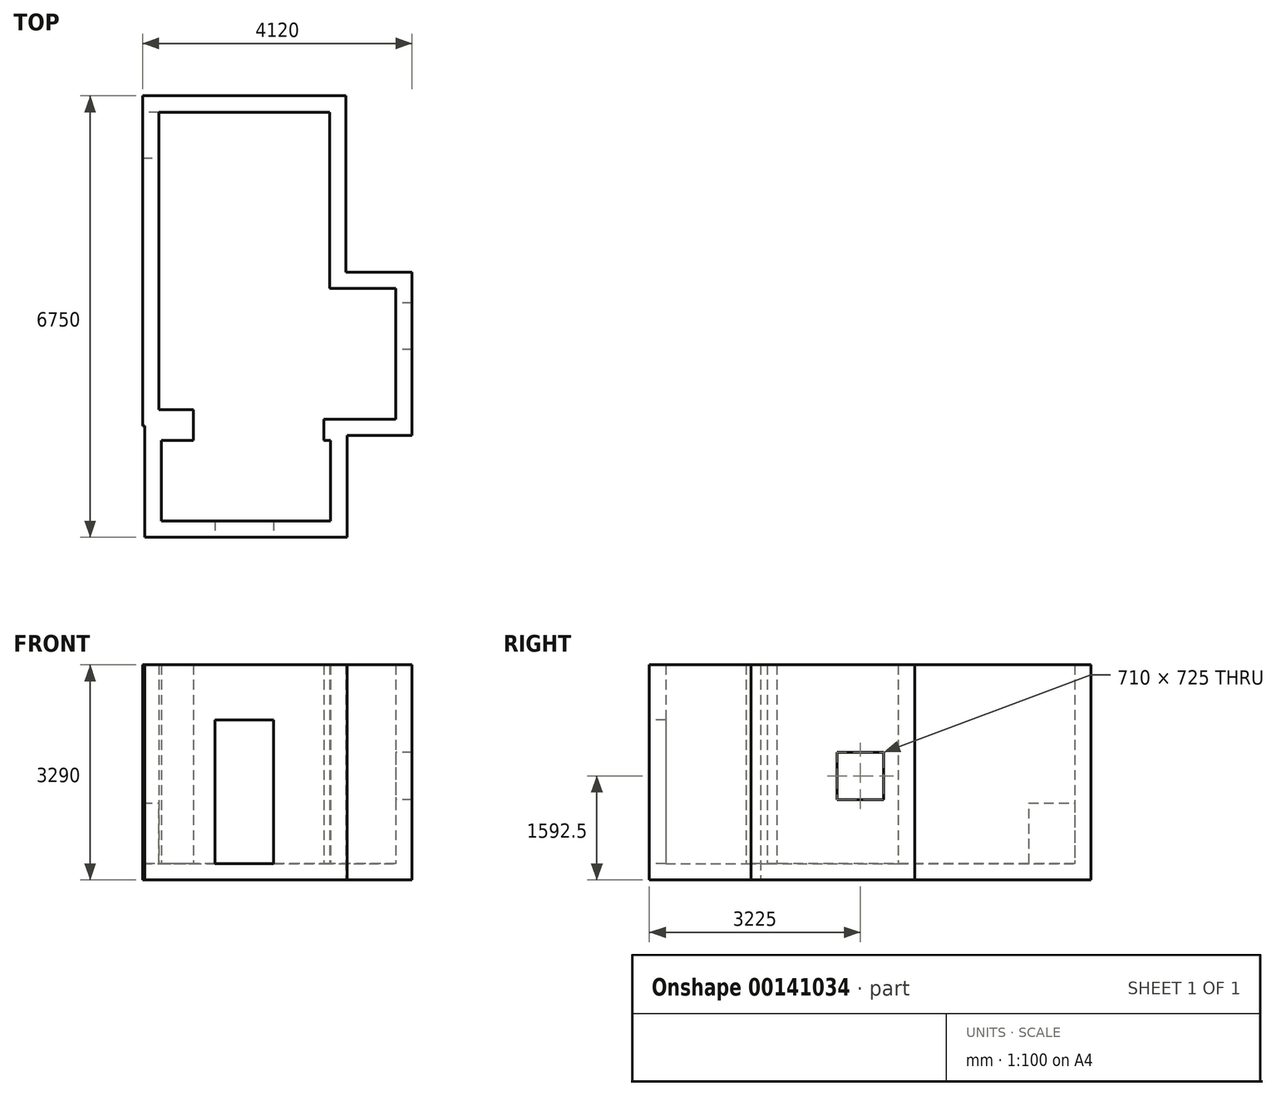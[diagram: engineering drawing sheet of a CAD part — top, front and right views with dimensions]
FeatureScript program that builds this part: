
annotation { "Feature Type Name" : "Feature", "Feature Type Description" : "" }
export const myFeature = defineFeature(function(context is Context, id is Id, definition is map)
    precondition{}
    {
        {
            var Q0;
            Q0=qCreatedBy(makeId("Top.planeOp"),FACE);
            var sketch = newSketch(context, id + "F0", { "sketchPlane" : qUnion([Q0])});
            skLineSegment(sketch, "E0", {"start": v(0, 0) * mm, "end": v(1649.99, 0) * mm});
            skLineSegment(sketch, "E1", {"start": v(1649.99, 0) * mm, "end": v(1649.99, 1230) * mm});
            skLineSegment(sketch, "E2", {"start": v(1649.99, 1230) * mm, "end": v(1544.99, 1230) * mm});
            skLineSegment(sketch, "E3", {"start": v(1544.99, 1230) * mm, "end": v(1544.99, 1555) * mm});
            skLineSegment(sketch, "E4", {"start": v(1544.99, 1555) * mm, "end": v(2644.99, 1555) * mm});
            skLineSegment(sketch, "E5", {"start": v(2644.99, 1555) * mm, "end": v(2644.99, 3555) * mm});
            skLineSegment(sketch, "E6", {"start": v(2644.99, 3555) * mm, "end": v(1634.99, 3555) * mm});
            skLineSegment(sketch, "E7", {"start": v(1634.99, 3555) * mm, "end": v(1634.99, 6250) * mm});
            skLineSegment(sketch, "E8", {"start": v(1634.99, 6250) * mm, "end": v(-975.01, 6250) * mm});
            skLineSegment(sketch, "E9", {"start": v(-975.01, 6250) * mm, "end": v(-975.01, 1700) * mm});
            skLineSegment(sketch, "E10", {"start": v(-975.01, 1700) * mm, "end": v(-450.01, 1700) * mm});
            skLineSegment(sketch, "E11", {"start": v(-450.01, 1700) * mm, "end": v(-450.01, 1230) * mm});
            skLineSegment(sketch, "E12", {"start": v(-450.01, 1230) * mm, "end": v(-940.01, 1230) * mm});
            skLineSegment(sketch, "E13", {"start": v(-940.01, 1230) * mm, "end": v(-940.01, 0) * mm});
            skLineSegment(sketch, "E14", {"start": v(-940.01, 0) * mm, "end": v(0, 0) * mm});
            skSolve(sketch);
        }
        {
            var Q0;
            Q0=qSketchRegion(id+"F0",true);
            extrude(context, id + "F1", {"entities" : qUnion([Q0]), "depth" : 3040 * mm});
        }
        {
            var Q0;
            Q0=makeQuery(id+"F1.opExtrude","CAP_FACE",FACE,{"disambiguationData":[OSD([sQuery(id+"F0.wireOp",EDGE,"E0"),sQuery(id+"F0.wireOp",EDGE,"E1"),sQuery(id+"F0.wireOp",EDGE,"E2"),sQuery(id+"F0.wireOp",EDGE,"E3"),sQuery(id+"F0.wireOp",EDGE,"E4"),sQuery(id+"F0.wireOp",EDGE,"E5"),sQuery(id+"F0.wireOp",EDGE,"E6"),sQuery(id+"F0.wireOp",EDGE,"E7"),sQuery(id+"F0.wireOp",EDGE,"E8"),sQuery(id+"F0.wireOp",EDGE,"E9"),sQuery(id+"F0.wireOp",EDGE,"E10"),sQuery(id+"F0.wireOp",EDGE,"E11"),sQuery(id+"F0.wireOp",EDGE,"E12"),sQuery(id+"F0.wireOp",EDGE,"E13"),sQuery(id+"F0.wireOp",EDGE,"E14")])],"isStart":false});
            shell(context, id + "F2", {"entities" : qUnion([Q0]), "thickness" : 250 * mm, "oppositeDirection" : true});
        }
        {
            var Q0;
            Q0=makeQuery(id+"F2.opShell","OFFSET_FACE",FACE,{"disambiguationData":[OSD([sQuery(id+"F0.wireOp",EDGE,"E5")])]});
            var sketch = newSketch(context, id + "F3", { "sketchPlane" : qUnion([Q0])});
            skLineSegment(sketch, "E15.bottom", {"start": v(-3330, 1705) * mm, "end": v(-2620, 1705) * mm});
            skLineSegment(sketch, "E15.top", {"start": v(-3330, 980) * mm, "end": v(-2620, 980) * mm});
            skLineSegment(sketch, "E15.left", {"start": v(-3330, 1705) * mm, "end": v(-3330, 980) * mm});
            skLineSegment(sketch, "E15.right", {"start": v(-2620, 1705) * mm, "end": v(-2620, 980) * mm});
            skSolve(sketch);
        }
        {
            var Q0;
            Q0=qSketchRegion(id+"F3",true);
            extrude(context, id + "F4", {"entities" : qUnion([Q0]), "operationType" : NewBodyOperationType.REMOVE, "endBound" : BoundingType.THROUGH_ALL, "oppositeDirection" : true, "depth" : 20 * mm});
        }
        {
            var Q0;
            Q0=makeQuery(id+"F1.opExtrude","SWEPT_FACE",FACE,{"disambiguationData":[OSD([sQuery(id+"F0.wireOp",EDGE,"E0"),sQuery(id+"F0.wireOp",EDGE,"E14")])]});
            var sketch = newSketch(context, id + "F5", { "sketchPlane" : qUnion([Q0])});
            skLineSegment(sketch, "E16.bottom", {"start": v(-120.01, 0) * mm, "end": v(779.99, 0) * mm});
            skLineSegment(sketch, "E16.top", {"start": v(-120.01, 2200) * mm, "end": v(779.99, 2200) * mm});
            skLineSegment(sketch, "E16.left", {"start": v(-120.01, 0) * mm, "end": v(-120.01, 2200) * mm});
            skLineSegment(sketch, "E16.right", {"start": v(779.99, 0) * mm, "end": v(779.99, 2200) * mm});
            skSolve(sketch);
        }
        {
            var Q0;
            Q0=qSketchRegion(id+"F5",true);
            extrude(context, id + "F6", {"entities" : qUnion([Q0]), "operationType" : NewBodyOperationType.REMOVE, "oppositeDirection" : true, "depth" : 500 * mm});
        }
        {
            var Q0;
            Q0=makeQuery(id+"F2.opShell","OFFSET_FACE",FACE,{"disambiguationData":[OSD([sQuery(id+"F0.wireOp",EDGE,"E9")])]});
            var sketch = newSketch(context, id + "F7", { "sketchPlane" : qUnion([Q0])});
            skLineSegment(sketch, "E17.bottom", {"start": v(5550, 0) * mm, "end": v(6250, 0) * mm});
            skLineSegment(sketch, "E17.top", {"start": v(5550, 930) * mm, "end": v(6250, 930) * mm});
            skLineSegment(sketch, "E17.left", {"start": v(5550, 0) * mm, "end": v(5550, 930) * mm});
            skLineSegment(sketch, "E17.right", {"start": v(6250, 0) * mm, "end": v(6250, 930) * mm});
            skSolve(sketch);
        }
        {
            var Q0;
            Q0=qSketchRegion(id+"F7",true);
            extrude(context, id + "F8", {"entities" : qUnion([Q0]), "operationType" : NewBodyOperationType.REMOVE, "endBound" : BoundingType.THROUGH_ALL, "oppositeDirection" : true, "depth" : 25 * mm});
        }
    });
